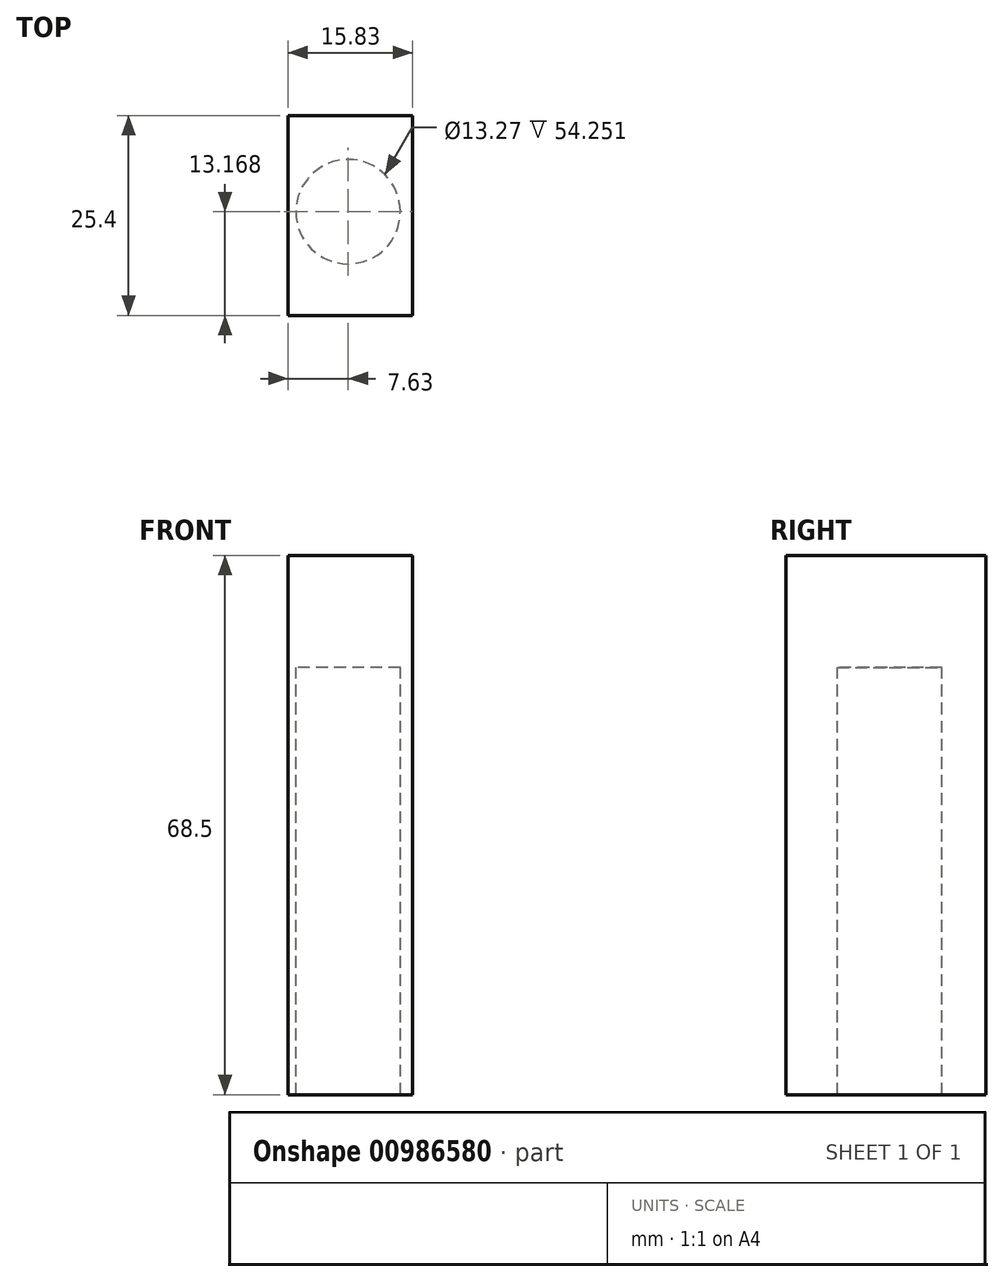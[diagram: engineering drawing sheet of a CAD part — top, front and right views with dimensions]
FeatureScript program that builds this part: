
annotation { "Feature Type Name" : "Feature", "Feature Type Description" : "" }
export const myFeature = defineFeature(function(context is Context, id is Id, definition is map)
    precondition{}
    {
        {
            var Q0;
            Q0=qCreatedBy(makeId("Front.planeOp"),FACE);
            var sketch = newSketch(context, id + "F0", { "sketchPlane" : qUnion([Q0])});
            skLineSegment(sketch, "E0.bottom", {"start": v(-7.63, -54.25) * mm, "end": v(8.2, -54.25) * mm});
            skLineSegment(sketch, "E0.top", {"start": v(-7.63, 14.25) * mm, "end": v(8.2, 14.25) * mm});
            skLineSegment(sketch, "E0.left", {"start": v(-7.63, -54.25) * mm, "end": v(-7.63, 14.25) * mm});
            skLineSegment(sketch, "E0.right", {"start": v(8.2, -54.25) * mm, "end": v(8.2, 14.25) * mm});
            skSolve(sketch);
        }
        {
            var Q0;
            Q0 = qSketchRegion(id + "F0", true);
            extrude(context, id + "F1", {"entities" : qUnion([Q0]), "depth" : 25.4 * mm, "offsetDistance" : 25.4 * mm});
        }
        {
            var Q0;
            Q0=qCreatedBy(makeId("Top.planeOp"),FACE);
            var sketch = newSketch(context, id + "F2", { "sketchPlane" : qUnion([Q0])});
            skCircle(sketch, "E1", {"center": v(0, -12.23) * mm, "radius": 6.63 * mm});
            skSolve(sketch);
        }
        {
            var Q0;
            Q0 = qSketchRegion(id + "F2", true);
            extrude(context, id + "F3", {"entities" : qUnion([Q0]), "operationType" : NewBodyOperationType.REMOVE, "oppositeDirection" : true, "depth" : 76.2 * mm, "offsetDistance" : 25.4 * mm});
        }
    });
